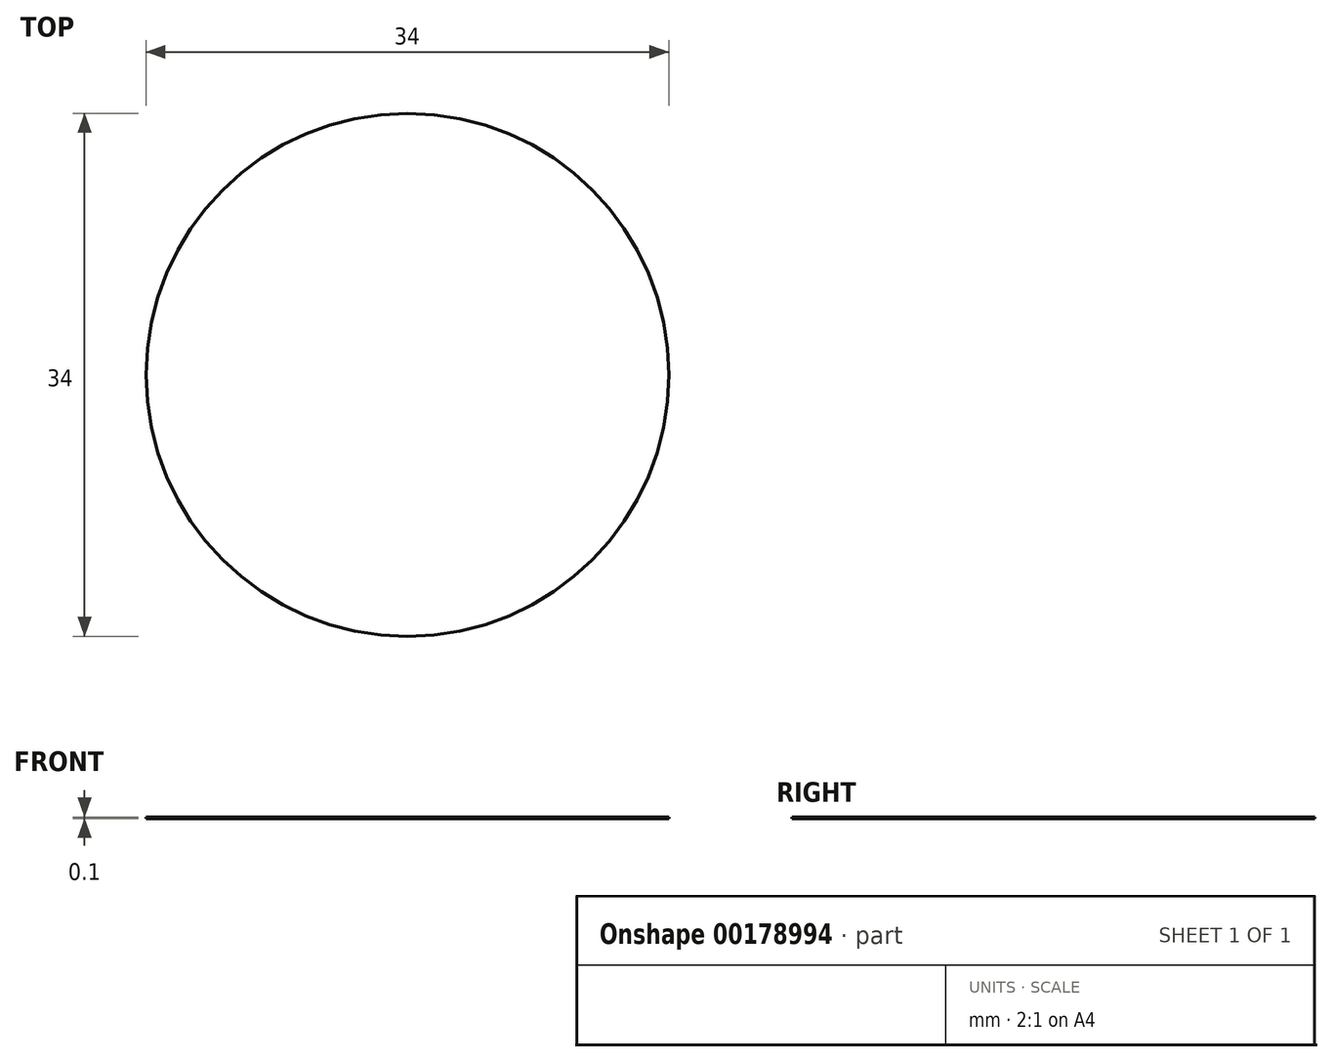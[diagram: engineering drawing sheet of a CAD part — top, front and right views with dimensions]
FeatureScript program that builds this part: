
annotation { "Feature Type Name" : "Feature", "Feature Type Description" : "" }
export const myFeature = defineFeature(function(context is Context, id is Id, definition is map)
    precondition{}
    {
        {
            var Q0;
            Q0=qCreatedBy(makeId("Top.planeOp"),FACE);
            var sketch = newSketch(context, id + "F0", { "sketchPlane" : qUnion([Q0])});
            skCircle(sketch, "E0", {"center": v(0, 0) * mm, "radius": 17 * mm});
            skSolve(sketch);
        }
        {
            var Q0;
            Q0 = qSketchRegion(id + "F0", true);
            extrude(context, id + "F1", {"entities" : qUnion([Q0]), "depth" : .1 * mm});
        }
    });
